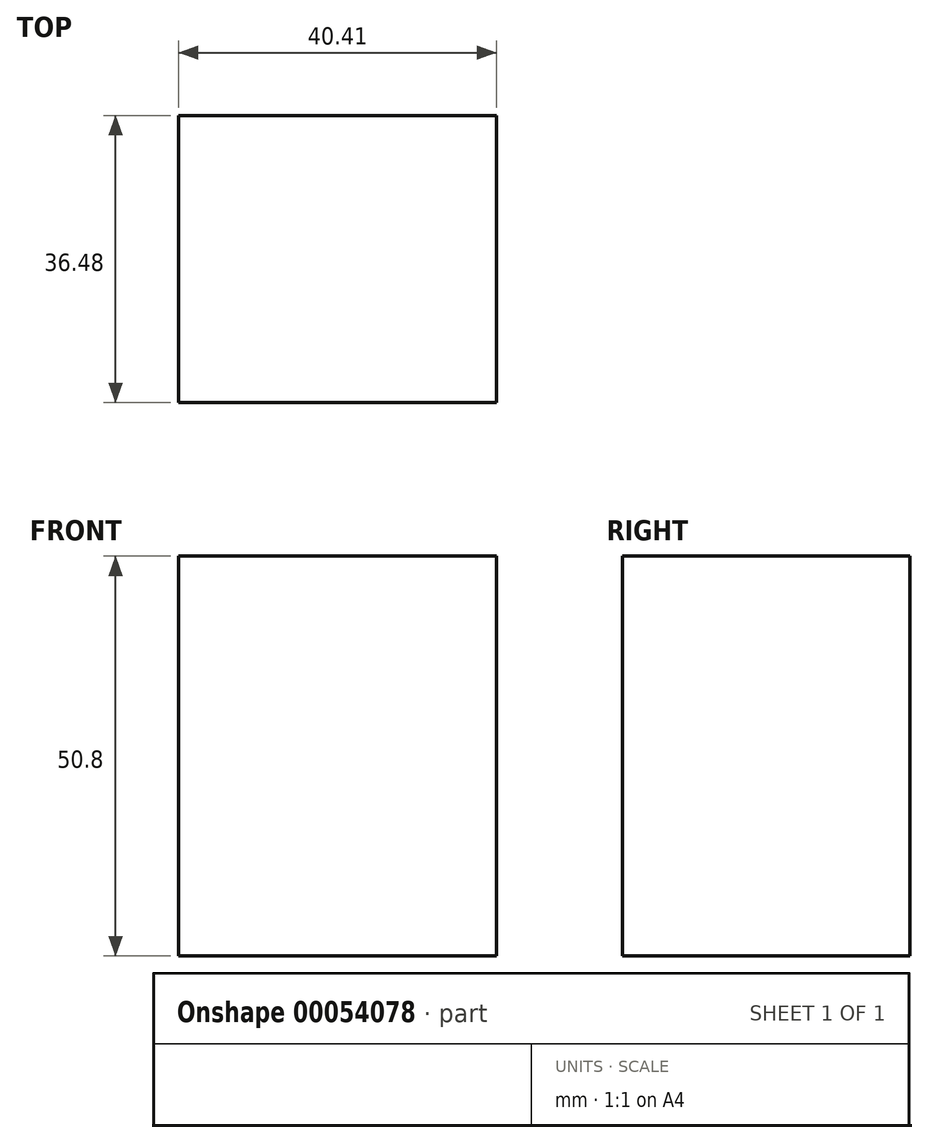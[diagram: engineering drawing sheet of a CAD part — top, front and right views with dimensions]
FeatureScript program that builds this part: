
annotation { "Feature Type Name" : "Feature", "Feature Type Description" : "" }
export const myFeature = defineFeature(function(context is Context, id is Id, definition is map)
    precondition{}
    {
        {
            var Q0;
            Q0=qCreatedBy(makeId("Top.planeOp"),FACE);
            var sketch = newSketch(context, id + "F0", { "sketchPlane" : qUnion([Q0])});
            skLineSegment(sketch, "E0", {"start": v(-53.8, 28.75) * mm, "end": v(-53.8, 65.23) * mm});
            skLineSegment(sketch, "E1", {"start": v(-53.8, 65.23) * mm, "end": v(-13.4, 65.23) * mm});
            skLineSegment(sketch, "E2", {"start": v(-13.4, 65.23) * mm, "end": v(-13.4, 28.06) * mm});
            skLineSegment(sketch, "E3", {"start": v(-53.8, 28.75) * mm, "end": v(-13.4, 28.75) * mm});
            skSolve(sketch);
        }
        {
            var Q0;
            Q0=makeQuery(id+"F0.imprint","IMPRINT",FACE,{"disambiguationData":[TD([[makeQuery(id+"F0.imprint","IMPRINT",EDGE,{"derivedFrom":sQuery(id+"F0.wireOp",EDGE,"E0")}),-1.0]])]});
            extrude(context, id + "F1", {"entities" : qUnion([Q0]), "depth" : 50.8 * mm});
        }
    });
